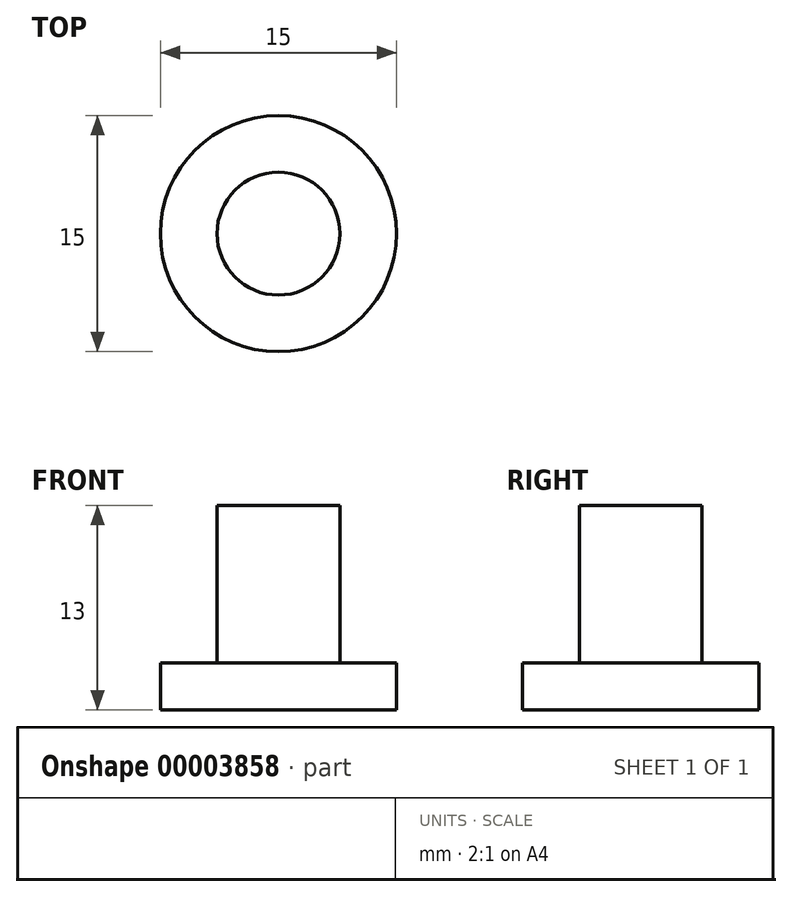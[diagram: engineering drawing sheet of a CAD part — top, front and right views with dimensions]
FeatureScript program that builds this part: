
annotation { "Feature Type Name" : "Feature", "Feature Type Description" : "" }
export const myFeature = defineFeature(function(context is Context, id is Id, definition is map)
    precondition{}
    {
        {
            var Q0;
            Q0=qCreatedBy(makeId("Top.planeOp"),FACE);
            var sketch = newSketch(context, id + "F0", { "sketchPlane" : qUnion([Q0])});
            skCircle(sketch, "E0", {"center": v(-91.21, -59.44) * mm, "radius": 3.9 * mm});
            skSolve(sketch);
        }
        {
            var Q0;
            Q0=makeQuery(id+"F0.imprint","IMPRINT",FACE,{"disambiguationData":[TD([[makeQuery(id+"F0.imprint","IMPRINT",EDGE,{"derivedFrom":sQuery(id+"F0.wireOp",EDGE,"E0")}),1.0]])]});
            extrude(context, id + "F1", {"entities" : qUnion([Q0]), "depth" : 10 * mm});
        }
        {
            var Q0;
            Q0=makeQuery(id+"F1.opExtrude","CAP_FACE",FACE,{"disambiguationData":[OSD([sQuery(id+"F0.wireOp",EDGE,"E0")])],"isStart":true});
            var sketch = newSketch(context, id + "F2", { "sketchPlane" : qUnion([Q0])});
            skCircle(sketch, "E1", {"center": v(-91.21, 59.44) * mm, "radius": 7.5 * mm});
            skSolve(sketch);
        }
        {
            var Q0;
            {var subQ0=makeQuery(id+"F2.imprint","IMPRINT",EDGE,{"derivedFrom":makeQuery(id+"F1.opExtrude","CAP_EDGE",EDGE,{"disambiguationData":[OSD([sQuery(id+"F0.wireOp",EDGE,"E0")])],"isStart":true})});Q0=qUnion([makeQuery(id+"F2.imprint","IMPRINT",FACE,{"disambiguationData":[TD([[makeQuery(id+"F2.imprint","IMPRINT",EDGE,{"derivedFrom":sQuery(id+"F2.wireOp",EDGE,"E1")}),1.0]])]}),makeQuery(id+"F2.imprint","IMPRINT",FACE,{"disambiguationData":[TD([[subQ0,-1.0]])]})]);}
            extrude(context, id + "F3", {"entities" : qUnion([Q0]), "operationType" : NewBodyOperationType.ADD, "depth" : 3 * mm});
        }
    });
